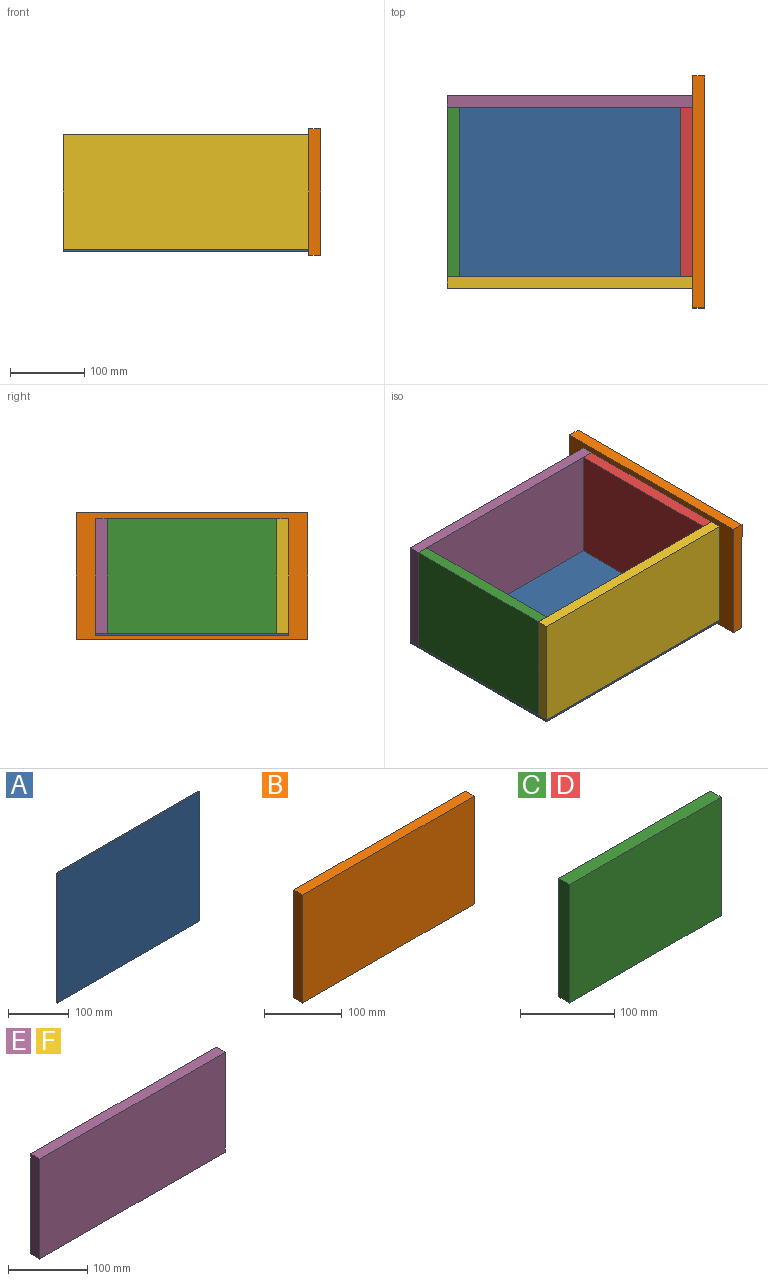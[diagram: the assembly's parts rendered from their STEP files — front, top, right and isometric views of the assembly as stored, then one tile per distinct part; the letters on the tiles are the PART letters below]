
ASSEMBLY  parts=6 mates=5
PART A: 6 faces, bbox 330x3x260 mm
  f0: plane 260x3mm, normal (-1,0,0), area 780mm2, adj f1,f3,f4,f5
  f1: plane 330x3mm, normal (0,0,-1), area 990mm2, adj f0,f2,f4,f5
  f2: plane 260x3mm, normal (1,0,0), area 780mm2, adj f1,f3,f4,f5
  f3: plane 330x3mm, normal (0,0,1), area 990mm2, adj f0,f2,f4,f5
  f4: plane 330x260mm, normal (0,-1,0), area 85800mm2, adj f0,f1,f2,f3
  f5: plane 330x260mm, normal (0,1,0), area 85800mm2, adj f0,f1,f2,f3
PART B: 6 faces, bbox 312x16x170 mm
  f0: plane 312x16mm, normal (0,0,1), area 4992mm2, adj f1,f3,f4,f5
  f1: plane 170x16mm, normal (-1,0,0), area 2720mm2, adj f0,f2,f4,f5
  f2: plane 312x16mm, normal (0,0,-1), area 4992mm2, adj f1,f3,f4,f5
  f3: plane 170x16mm, normal (1,0,0), area 2720mm2, adj f0,f2,f4,f5
  f4: plane 312x170mm, normal (0,-1,0), area 53040mm2, adj f0,f1,f2,f3
  f5: plane 312x170mm, normal (0,1,0), area 53040mm2, adj f0,f1,f2,f3
PART C: 6 faces, bbox 228x16x154 mm
  f0: plane 228x16mm, normal (0,0,1), area 3648mm2, adj f1,f3,f4,f5
  f1: plane 154x16mm, normal (-1,0,0), area 2464mm2, adj f0,f2,f4,f5
  f2: plane 228x16mm, normal (0,0,-1), area 3648mm2, adj f1,f3,f4,f5
  f3: plane 154x16mm, normal (1,0,0), area 2464mm2, adj f0,f2,f4,f5
  f4: plane 228x154mm, normal (0,-1,0), area 35112mm2, adj f0,f1,f2,f3
  f5: plane 228x154mm, normal (0,1,0), area 35112mm2, adj f0,f1,f2,f3
PART D: same geometry as C
PART E: 6 faces, bbox 330x16x154 mm
  f0: plane 154x16mm, normal (-1,0,0), area 2464mm2, adj f1,f3,f4,f5
  f1: plane 330x16mm, normal (0,0,-1), area 5280mm2, adj f0,f2,f4,f5
  f2: plane 154x16mm, normal (1,0,0), area 2464mm2, adj f1,f3,f4,f5
  f3: plane 330x16mm, normal (0,0,1), area 5280mm2, adj f0,f2,f4,f5
  f4: plane 330x154mm, normal (0,-1,0), area 50820mm2, adj f0,f1,f2,f3
  f5: plane 330x154mm, normal (0,1,0), area 50820mm2, adj f0,f1,f2,f3
PART F: same geometry as E
PLACE A rot(axis=(-1,0,0),90deg) t=(-417.31,-258.13,-74.7)mm
PLACE B rot(axis=(0.71,0.71,0),180deg) t=(-71.31,-284.13,-79.7)mm
PLACE C rot(axis=(0,0,-1),90deg) t=(-401.31,-14.13,82.3)mm
PLACE D rot(axis=(0.71,0.71,0),180deg) t=(-87.31,-242.13,-71.7)mm
PLACE E t=(-417.31,1.87,-71.7)mm
PLACE F t=(-417.31,-242.13,-71.7)mm
MATE fastened D.f1 <-> F.f5  axis (0,-1,0) through (-87.31,-242.13,5.3)mm
MATE fastened C.f1 <-> E.f4  axis (0,1,0) through (-417.31,-14.13,5.3)mm
MATE fastened D.f3 <-> E.f4  axis (0,1,0) through (-87.31,-14.13,5.3)mm
MATE fastened A.f4 <-> F.f1  axis (0,0,1) through (-417.31,-258.13,-71.7)mm
MATE fastened D.f5 <-> B.f4  axis (1,0,0) through (-87.31,-128.13,5.3)mm
